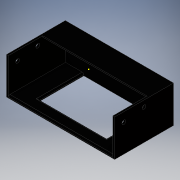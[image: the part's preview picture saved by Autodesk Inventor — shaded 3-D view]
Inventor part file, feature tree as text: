
AUTODESK INVENTOR PART (.ipt)
format: ipt  version: 2016 (Build 200138000, 138)  size: 203,264 bytes
history: native  units: in
note: dims shown in document units (in); Inventor stores cm internally (conversion verified against a paired STEP export)
features: sketch x10, extrude x7, fillet x4, hole x2, projected_geometry x1
ambient origin geometry x8: Origin, YZ Plane, XZ Plane, XY Plane, X Axis, Y Axis, Z Axis, Center Point
bodies: Solid1 (feature_tree)
feature tree (24):
  sketch  "Sketch1"  dims[d0=5.0in d1=8.8189in]
  extrude  "Extrusion1"  Depth=8.8189in
  extrude  "Extrusion2"  Depth=3.0in
  extrude  "Extrusion3"  Depth=2.9in TaperAngle=0.0deg
  extrude  "Extrusion4"  Depth=1.5in TaperAngle=0.0deg
  extrude  "Extrusion5"  Depth=0.2in
  extrude  "Extrusion6"  Depth=0.2in TaperAngle=0.0deg
  extrude  "Extrusion7"  Depth=5.5in TaperAngle=0.0deg
  fillet  "Fillet1"  Radius=2.8in
  fillet  "Fillet2"  Radius=0.125in
  fillet  "Fillet3"  Radius=0.125in
  hole  "Hole1"  [1 undecoded]
  fillet  "Fillet4"  Radius=0.125in
  hole  "Hole2"  [1 undecoded]
  sketch  "Sketch2"  dims[d2=3.0in d3=0.0in d4=4.7in]
  sketch  "Sketch3"  dims[d5=8.5in d6=2.9in d7=0.0in]
  sketch  "Sketch4"  dims[d8=0.2in d9=1.5in d10=0.0in]
  sketch  "Sketch5"  dims[d11=4.7in d12=0.2in]
  sketch  "Sketch7"  dims[d13=1.5in d14=0.0in d15=0.2in d16=0.0in]
  projected_geometry  "Projected Loop1"
  sketch  "Sketch8"  dims[d17=1.0in d18=5.5in d19=0.0in d20=2.8in d21=0.0in d22=0.125in d23=0.125in]
  sketch  "Sketch9"  dims[d24=0.125in d27=0.315in]
  sketch  "Sketch10"  dims[d28=0.315in d29=0.75in d30=0.375in d31=0.25in d32=0.5635in d33=1.0in d34=0.8108in d35=0.125in]
  sketch  "Sketch11"  dims[d37=0.315in d38=0.75in d39=0.375in d40=0.25in d41=0.5635in d42=1.0in d43=0.8108in]
note: 2 required parameter values undecoded (feature->parameter linkage not recoverable at this tier; creation-order binding heuristic only, values carry confidence <= 0.55)
